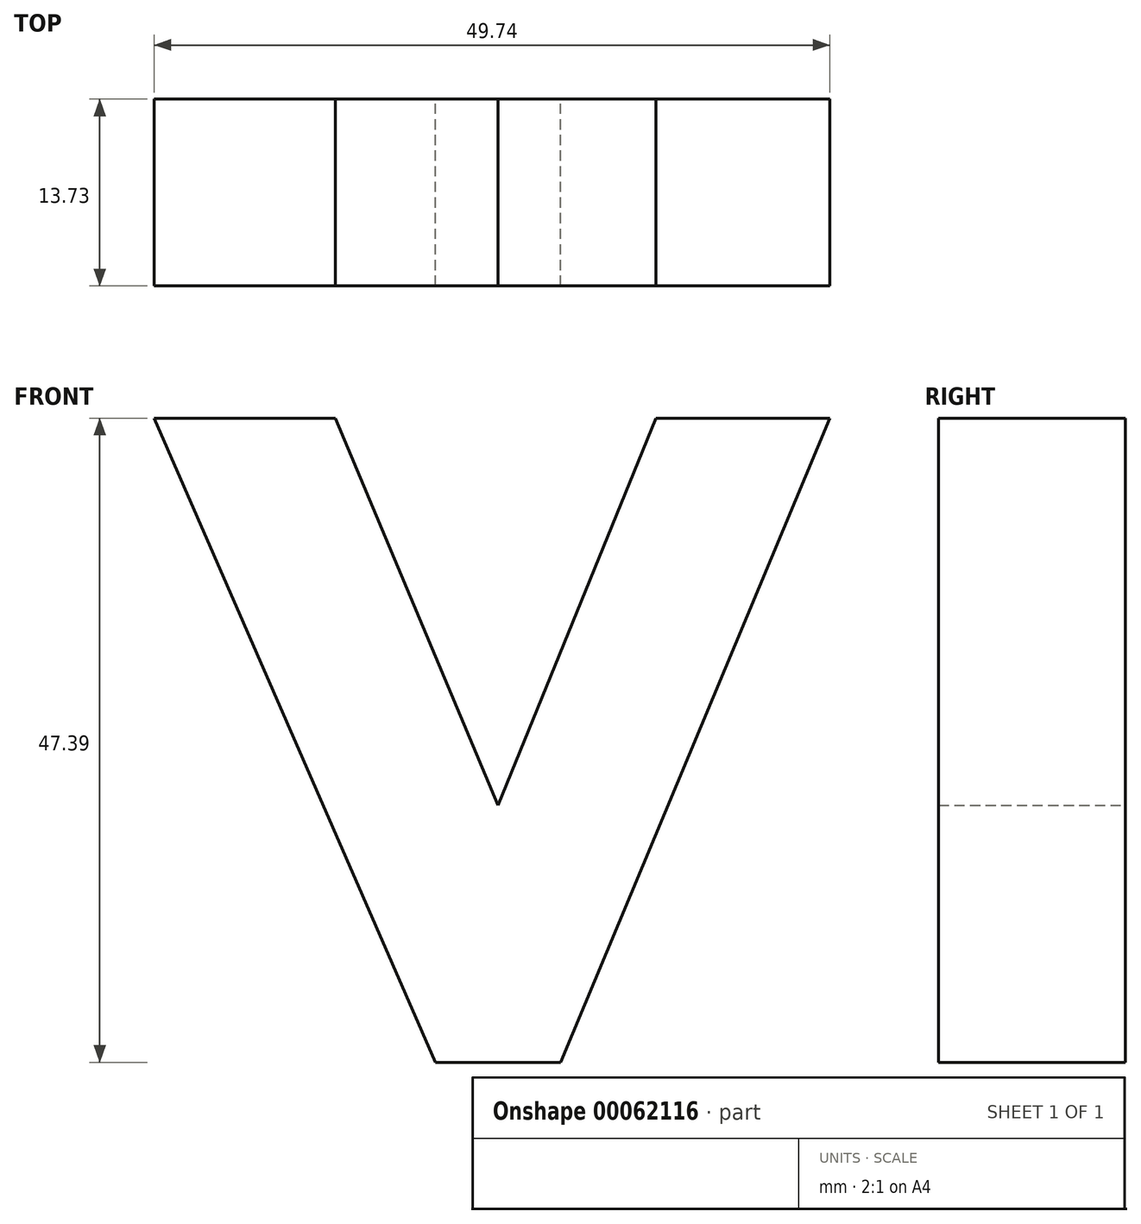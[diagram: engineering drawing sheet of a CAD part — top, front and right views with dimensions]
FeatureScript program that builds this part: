
annotation { "Feature Type Name" : "Feature", "Feature Type Description" : "" }
export const myFeature = defineFeature(function(context is Context, id is Id, definition is map)
    precondition{}
    {
        {
            var Q0;
            Q0=qCreatedBy(makeId("Front.planeOp"),FACE);
            var sketch = newSketch(context, id + "F0", { "sketchPlane" : qUnion([Q0])});
            skLineSegment(sketch, "E0", {"start": v(-4.6, 0) * mm, "end": v(4.6, 0) * mm});
            skLineSegment(sketch, "E1", {"start": v(4.6, 0) * mm, "end": v(24.42, 47.4) * mm});
            skLineSegment(sketch, "E2", {"start": v(24.42, 47.4) * mm, "end": v(11.62, 47.4) * mm});
            skLineSegment(sketch, "E3", {"start": v(11.62, 47.4) * mm, "end": v(0, 18.92) * mm});
            skLineSegment(sketch, "E4", {"start": v(0, 18.92) * mm, "end": v(-11.98, 47.4) * mm});
            skLineSegment(sketch, "E5", {"start": v(-11.98, 47.4) * mm, "end": v(-25.32, 47.4) * mm});
            skLineSegment(sketch, "E6", {"start": v(-25.32, 47.4) * mm, "end": v(-4.6, 0) * mm});
            skSolve(sketch);
        }
        {
            var Q0;
            Q0 = qSketchRegion(id + "F0", true);
            extrude(context, id + "F1", {"entities" : qUnion([Q0]), "depth" : 13.73 * mm});
        }
    });
